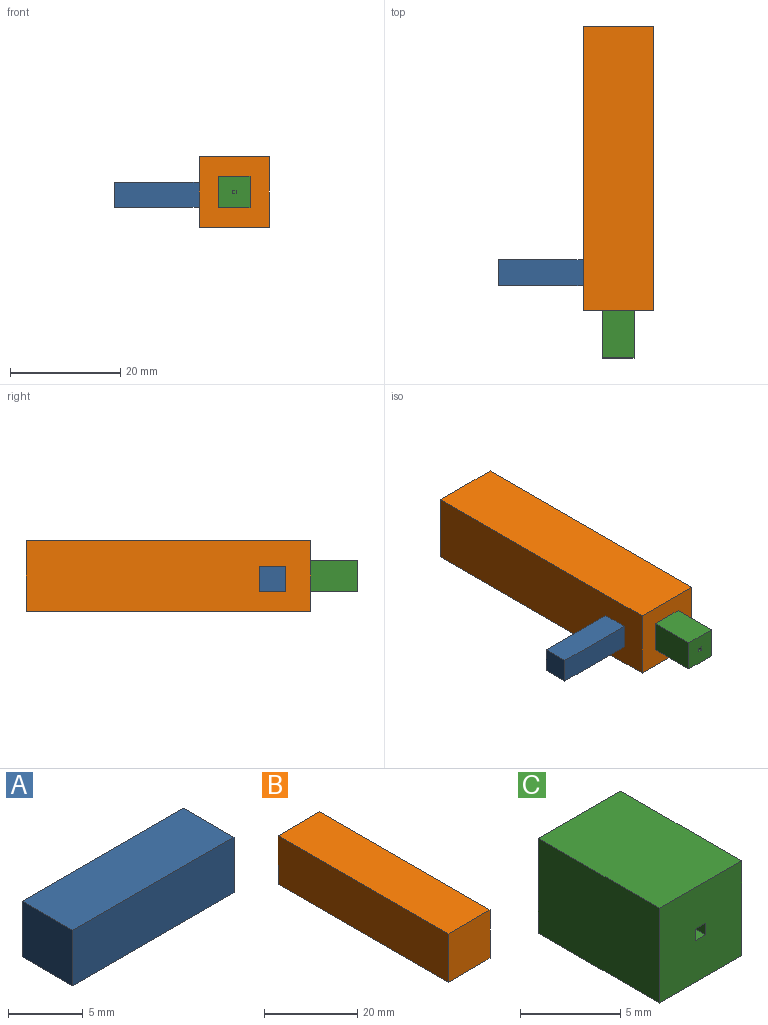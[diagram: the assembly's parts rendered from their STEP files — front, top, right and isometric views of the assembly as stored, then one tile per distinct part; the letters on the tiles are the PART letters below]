
ASSEMBLY  parts=3 mates=2
PART A: 6 faces, bbox 15.2x4.8x4.5 mm
  f0: plane 15.24x4.54mm, normal (0,-1,0), area 69.2mm2, adj f1,f3,f4,f5
  f1: plane 15.24x4.78mm, normal (0,0,-1), area 72.9mm2, adj f0,f2,f4,f5
  f2: plane 15.24x4.54mm, normal (0,1,0), area 69.2mm2, adj f1,f3,f4,f5
  f3: plane 15.24x4.78mm, normal (0,0,1), area 72.9mm2, adj f0,f2,f4,f5
  f4: plane 4.78x4.54mm, normal (1,0,0), area 21.7mm2, adj f0,f1,f2,f3
  f5: plane 4.78x4.54mm, normal (-1,0,0), area 21.7mm2, adj f0,f1,f2,f3
PART B: 6 faces, bbox 12.7x51.6x12.7 mm
  f0: plane 12.7x12.7mm, normal (0,-1,0), area 161.3mm2, adj f1,f3,f4,f5
  f1: plane 51.63x12.7mm, normal (1,0,0), area 655.7mm2, adj f0,f2,f4,f5
  f2: plane 12.7x12.7mm, normal (0,1,0), area 161.3mm2, adj f1,f3,f4,f5
  f3: plane 51.63x12.7mm, normal (-1,0,0), area 655.7mm2, adj f0,f2,f4,f5
  f4: plane 51.63x12.7mm, normal (0,0,1), area 655.7mm2, adj f0,f1,f2,f3
  f5: plane 51.63x12.7mm, normal (0,0,-1), area 655.7mm2, adj f0,f1,f2,f3
PART C: 11 faces, bbox 5.8x8.5x5.8 mm
  f0: plane 5.79x5.79mm, normal (0,-1,0), area 33mm2, adj f1,f3,f4,f5,f6,f8,f9,f10
  f1: plane 8.53x5.79mm, normal (1,0,0), area 49.4mm2, adj f0,f2,f4,f5
  f2: plane 5.79x5.79mm, normal (0,1,0), area 33.5mm2, adj f1,f3,f4,f5
  f3: plane 8.53x5.79mm, normal (-1,0,0), area 49.4mm2, adj f0,f2,f4,f5
  f4: plane 8.53x5.79mm, normal (0,0,1), area 49.4mm2, adj f0,f1,f2,f3
  f5: plane 8.53x5.79mm, normal (0,0,-1), area 49.4mm2, adj f0,f1,f2,f3
  f6: plane 5.99x0.71mm, normal (-1,0,0), area 4.3mm2, adj f0,f7,f9,f10
  f7: plane 0.71x0.71mm, normal (0,-1,0), area 0.5mm2, adj f6,f8,f9,f10
  f8: plane 5.99x0.71mm, normal (1,0,0), area 4.3mm2, adj f0,f7,f9,f10
  f9: plane 5.99x0.71mm, normal (0,0,-1), area 4.3mm2, adj f0,f6,f7,f8
  f10: plane 5.99x0.71mm, normal (0,0,1), area 4.3mm2, adj f0,f6,f7,f8
PLACE A t=(4.57,7.34,0.01)mm
PLACE B t=(4.57,7.37,0)mm
PLACE C t=(4.48,7.37,0.1)mm
MATE fastened A.f4 <-> B.f3  axis (1,0,0) through (-2.37,14.84,5.87)mm
MATE fastened C.f2 <-> B.f0  axis (0,1,0) through (3.98,7.93,6.35)mm
